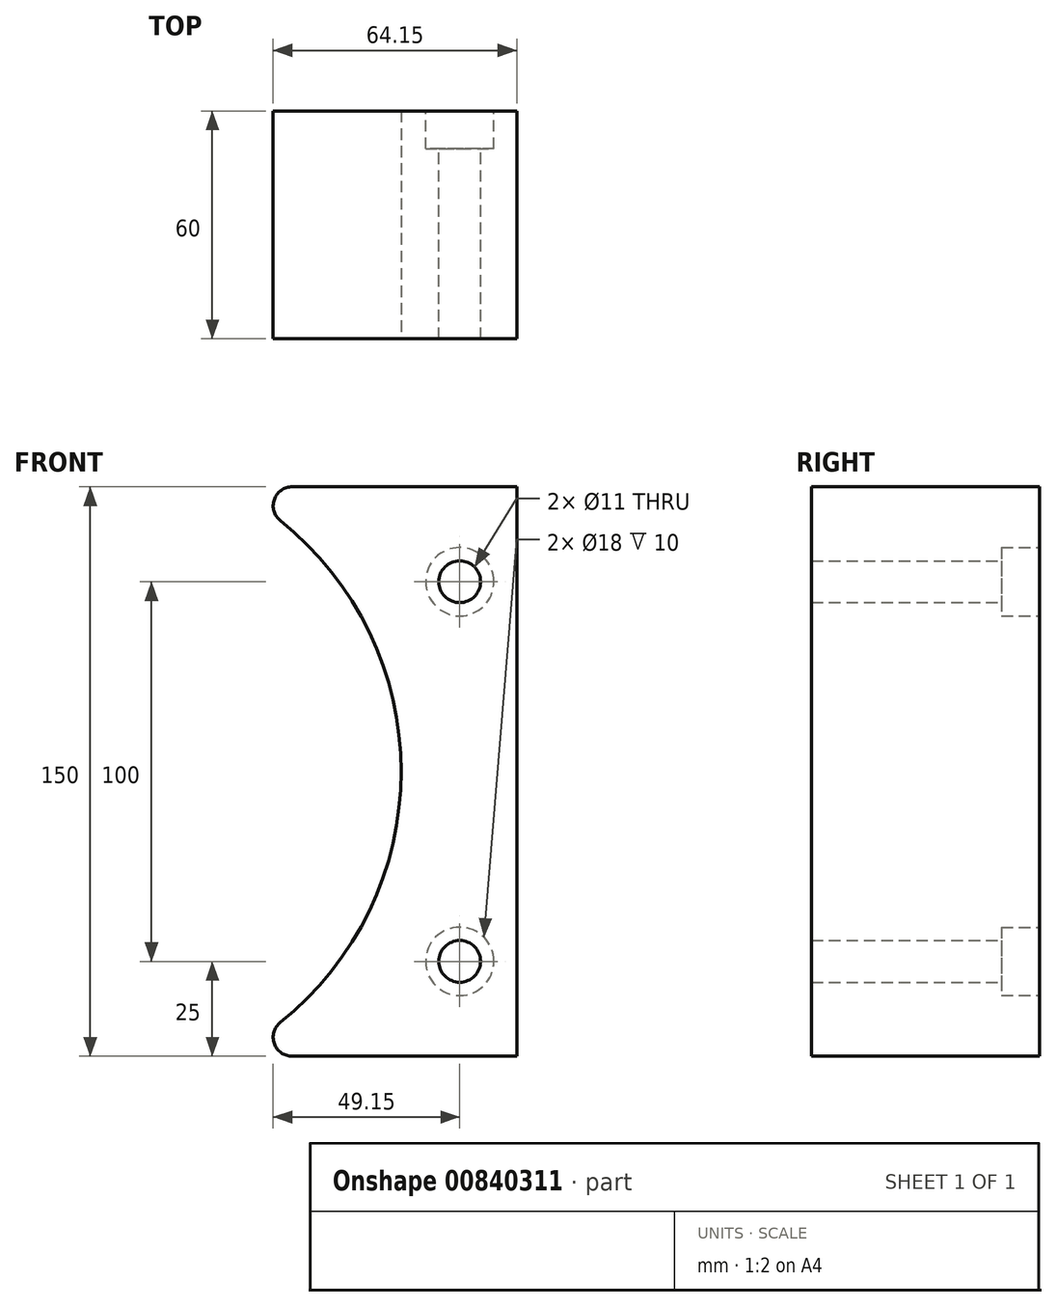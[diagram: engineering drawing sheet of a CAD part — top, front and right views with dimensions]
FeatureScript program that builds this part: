
annotation { "Feature Type Name" : "Feature", "Feature Type Description" : "" }
export const myFeature = defineFeature(function(context is Context, id is Id, definition is map)
    precondition{}
    {
        {
            var Q0;
            Q0=qCreatedBy(makeId("Front.planeOp"),FACE);
            var sketch = newSketch(context, id + "F0", { "sketchPlane" : qUnion([Q0])});
            skLineSegment(sketch, "E0.bottom", {"start": v(-37.5, 75) * mm, "end": v(37.5, 75) * mm});
            skLineSegment(sketch, "E0.top", {"start": v(-37.5, -75) * mm, "end": v(37.5, -75) * mm});
            skLineSegment(sketch, "E0.left", {"start": v(-37.5, 75) * mm, "end": v(-37.5, -75) * mm});
            skLineSegment(sketch, "E0.right", {"start": v(37.5, 75) * mm, "end": v(37.5, -75) * mm});
            skPoint(sketch, "E0.middle", {"position": v(0, 0) * mm});
            skSolve(sketch);
        }
        {
            var Q0;
            Q0=qSketchRegion(id+"F0",true);
            extrude(context, id + "F1", {"entities" : qUnion([Q0]), "endBound" : BoundingType.SYMMETRIC, "depth" : 60 * mm, "offsetDistance" : 25 * mm});
        }
        {
            var Q0;
            Q0=makeQuery(id+"F1.opExtrude","CAP_FACE",FACE,{"disambiguationData":[OSD([sQuery(id+"F0.wireOp",EDGE,"E0.bottom"),sQuery(id+"F0.wireOp",EDGE,"E0.top"),sQuery(id+"F0.wireOp",EDGE,"E0.left"),sQuery(id+"F0.wireOp",EDGE,"E0.right")])],"isStart":false});
            var sketch = newSketch(context, id + "F2", { "sketchPlane" : qUnion([Q0])});
            skCircle(sketch, "E1", {"center": v(-77.5, 0) * mm, "radius": 84.55 * mm});
            skArc(sketch, "E2", {"start": v(-21.65, 75) * mm, "mid": v(-26.37, 71.65) * mm, "end": v(-24.77, 66.1) * mm});
            skArc(sketch, "E3", {"start": v(-24.77, -66.1) * mm, "mid": v(-26.37, -71.65) * mm, "end": v(-21.65, -75) * mm});
            skSolve(sketch);
        }
        {
            var Q0;
            Q0=qSketchRegion(id+"F2",true);
            var Q1;
            {var subQ0=sQuery(id+"F2.wireOp",EDGE,"E2");Q1=makeQuery(id+"F2.imprint","IMPRINT",FACE,{"disambiguationData":[TD([[makeQuery(id+"F2.imprint","IMPRINT",EDGE,{"derivedFrom":subQ0}),-1.0]])]});}
            var Q2;
            {var subQ0=sQuery(id+"F2.wireOp",EDGE,"E3");Q2=makeQuery(id+"F2.imprint","IMPRINT",FACE,{"disambiguationData":[TD([[makeQuery(id+"F2.imprint","IMPRINT",EDGE,{"derivedFrom":subQ0}),-1.0]])]});}
            extrude(context, id + "F3", {"entities" : qUnion([Q0, Q1, Q2]), "operationType" : NewBodyOperationType.REMOVE, "endBound" : BoundingType.THROUGH_ALL, "oppositeDirection" : true, "depth" : 25 * mm, "offsetDistance" : 25 * mm});
        }
        {
            var Q0;
            Q0=makeQuery(id+"F1.opExtrude","CAP_FACE",FACE,{"disambiguationData":[OSD([sQuery(id+"F0.wireOp",EDGE,"E0.bottom"),sQuery(id+"F0.wireOp",EDGE,"E0.top"),sQuery(id+"F0.wireOp",EDGE,"E0.left"),sQuery(id+"F0.wireOp",EDGE,"E0.right")])],"isStart":true});
            var sketch = newSketch(context, id + "F4", { "sketchPlane" : qUnion([Q0])});
            skPoint(sketch, "E4", {"position": v(-22.5, 50) * mm});
            skPoint(sketch, "E5", {"position": v(-22.5, -50) * mm});
            skSolve(sketch);
        }
        {
            var Q0;
            Q0=sQuery(id+"F4.wireOp",VERTEX,"E4");
            var Q1;
            Q1=sQuery(id+"F4.wireOp",VERTEX,"E5");
            var Q2;
            Q2=makeQuery(id+"F1.opExtrude","SWEPT_BODY",BODY,{"disambiguationData":[OSD([sQuery(id+"F0.wireOp",EDGE,"E0.bottom"),sQuery(id+"F0.wireOp",EDGE,"E0.top"),sQuery(id+"F0.wireOp",EDGE,"E0.left"),sQuery(id+"F0.wireOp",EDGE,"E0.right")])]});
            hole(context, id + "F5", {"style" : HoleStyle.C_BORE, "endStyle" : HoleEndStyle.THROUGH, "holeDiameter" : 11 * mm, "cBoreDiameter" : 18 * mm, "cBoreDepth" : 10 * mm, "majorDiameter" : 5 * mm, "isTappedThrough" : true, "tappedDepth" : 12 * mm, "tapClearance" : 3, "startFromSketch" : true, "locations" : qUnion([Q0, Q1]), "scope" : qUnion([Q2])});
        }
    });
